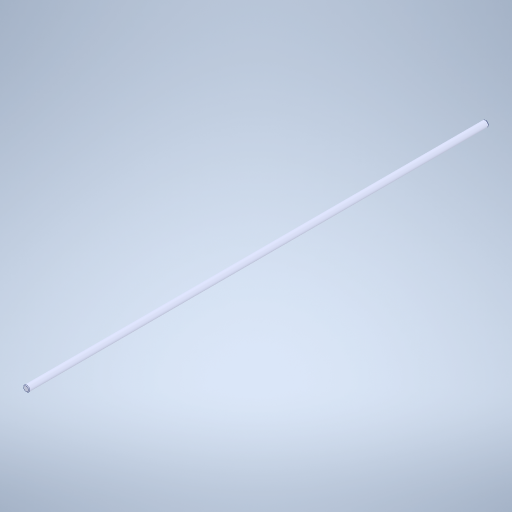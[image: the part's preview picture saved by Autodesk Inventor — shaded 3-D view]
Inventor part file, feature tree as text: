
AUTODESK INVENTOR PART (.ipt)
format: ipt  version: 2023 (Build 270158000, 158)  size: 261,632 bytes
history: mixed  units: in
note: dims shown in document units (in); Inventor stores cm internally (conversion verified against a paired STEP export)
features: chamfer x1, imported_body x1
ambient origin geometry x8: Origin, YZ Plane, XZ Plane, XY Plane, X Axis, Y Axis, Z Axis, Center Point
bodies: Solid1 (imported_parasolid)
feature tree (2):
  chamfer  "Chamfer1"  [1 undecoded]
  imported_body  NMx_Import_Brep_tag  [imported B-rep: ~5 faces, bbox_mm=[0.8, 0.0, 600.0]]
note: 1 required parameter value undecoded (feature->parameter linkage not recoverable at this tier; creation-order binding heuristic only, values carry confidence <= 0.55)
